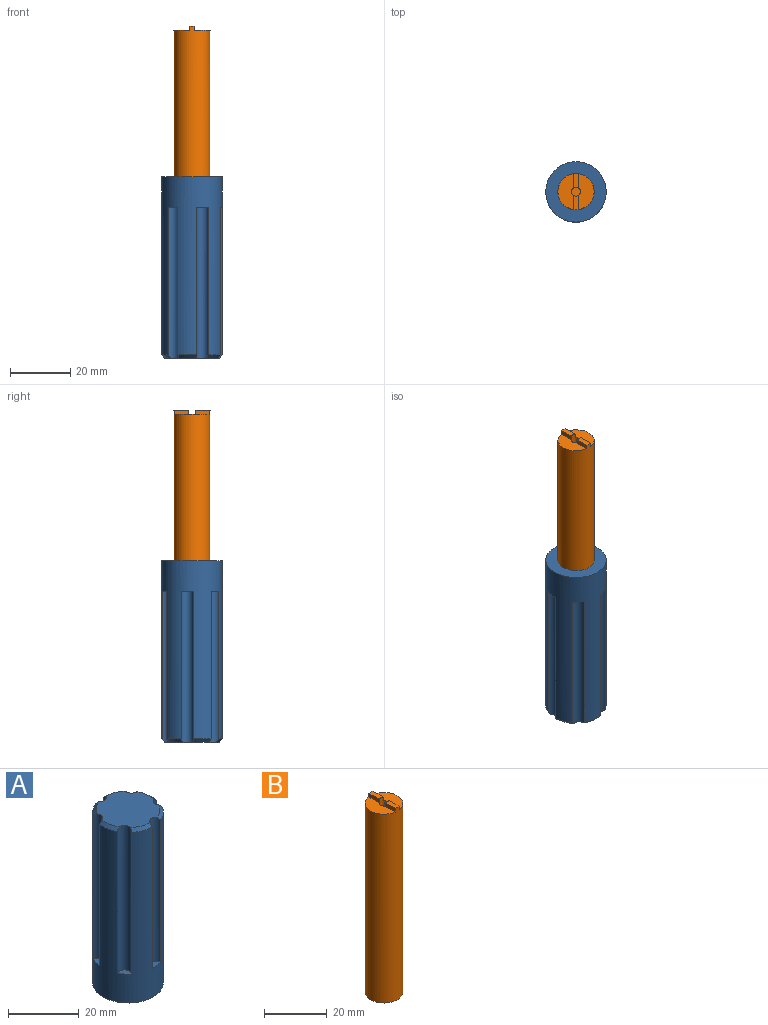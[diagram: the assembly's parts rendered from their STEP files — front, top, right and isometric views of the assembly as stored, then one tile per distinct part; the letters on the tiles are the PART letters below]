
ASSEMBLY  parts=2 mates=1
PART A: 23 faces, bbox 20x20x60 mm
  f0: cylinder r=10mm len=59mm, axis (0,0,-1), area 2529.1mm2, adj f2,f3,f4,f5,f6,f7,f8,f9
  f1: plane 18x18mm, normal (0,0,1), area 240.8mm2, adj f4,f6,f8,f10,f12,f14,f15,f16
  f2: plane 20x20mm, normal (0,0,-1), area 201.1mm2, adj f0,f21
  f3: plane 3.93x2.13mm, normal (0,0,1), area 6mm2, adj f0,f4
  f4: cylinder r=2mm len=50mm, axis (0,0,1), area 293.1mm2, adj f0,f1,f3,f16,f17
  f5: plane 3.41x3.11mm, normal (0,0,1), area 6mm2, adj f0,f6
  f6: cylinder r=2mm len=50mm, axis (0,0,1), area 293.1mm2, adj f0,f1,f5,f17,f18
  f7: plane 3.79x2.52mm, normal (0,0,1), area 6mm2, adj f0,f8
  f8: cylinder r=2mm len=50mm, axis (0,0,1), area 293.1mm2, adj f0,f1,f7,f18,f19
  f9: plane 3.93x2.13mm, normal (0,0,1), area 6mm2, adj f0,f10
  f10: cylinder r=2mm len=50mm, axis (0,0,1), area 293.1mm2, adj f0,f1,f9,f19,f20
  f11: plane 3.41x3.11mm, normal (0,0,1), area 6mm2, adj f0,f12
  f12: cylinder r=2mm len=50mm, axis (0,0,1), area 293.1mm2, adj f0,f1,f11,f15,f20
  f13: plane 3.79x2.52mm, normal (0,0,1), area 6mm2, adj f0,f14
  f14: cylinder r=2mm len=50mm, axis (0,0,1), area 293.1mm2, adj f0,f1,f13,f15,f16
  f15: cone r=9mm half-angle=45deg, axis (0,0,-1), area 8.8mm2, adj f0,f1,f12,f14
  f16: cone r=9mm half-angle=45deg, axis (0,0,-1), area 8.8mm2, adj f0,f1,f4,f14
  f17: cone r=9mm half-angle=45deg, axis (0,0,-1), area 8.8mm2, adj f0,f1,f4,f6
  f18: cone r=9mm half-angle=45deg, axis (0,0,-1), area 8.8mm2, adj f0,f1,f6,f8
  f19: cone r=9mm half-angle=45deg, axis (0,0,-1), area 8.8mm2, adj f0,f1,f8,f10
  f20: cone r=9mm half-angle=45deg, axis (0,0,-1), area 8.8mm2, adj f0,f1,f10,f12
  f21: cylinder r=6mm len=25mm, axis (0,0,-1), area 942.5mm2, adj f2,f22
  f22: plane 12x12mm, normal (0,0,-1), area 113.1mm2, adj f21
PART B: 12 faces, bbox 12x12x75 mm
  f0: cylinder r=6mm len=75mm, axis (0,0,-1), area 2779.6mm2, adj f1,f2,f4,f6,f7,f8,f9,f10
  f1: plane 4.78x1.75mm, normal (0,0,1), area 8mm2, adj f0,f3,f6,f9
  f2: plane 4.78x1.75mm, normal (0,0,1), area 8mm2, adj f0,f3,f7,f10
  f3: cylinder r=1.5mm len=12mm, axis (0,0,1), area 105.1mm2, adj f1,f2,f5,f6,f7,f8,f9,f10
  f4: plane 12x12mm, normal (0,0,-1), area 113.1mm2, adj f0
  f5: plane 3x3mm, normal (0,0,1), area 7.1mm2, adj f3
  f6: plane 4.72x1.4mm, normal (1,0,0), area 6.6mm2, adj f0,f1,f3,f8
  f7: plane 4.72x1.4mm, normal (1,0,0), area 6.6mm2, adj f0,f2,f3,f8
  f8: plane 11.87x5.13mm, normal (0,0,1), area 45mm2, adj f0,f3,f6,f7
  f9: plane 4.72x1.4mm, normal (-1,0,0), area 6.6mm2, adj f0,f1,f3,f11
  f10: plane 4.72x1.4mm, normal (-1,0,0), area 6.6mm2, adj f0,f2,f3,f11
  f11: plane 11.87x5.13mm, normal (0,0,1), area 45mm2, adj f0,f3,f9,f10
PLACE A rot(axis=(0.71,-0.71,0),180deg) t=(-32.08,-1.21,13.47)mm
PLACE B t=(-32.08,-1.21,-11.53)mm
MATE fastened A.f21 <-> B.f0  axis (0,0,1) through (-32.08,-1.21,-11.53)mm
